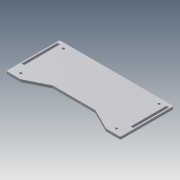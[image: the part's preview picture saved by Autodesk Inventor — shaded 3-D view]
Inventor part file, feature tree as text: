
AUTODESK INVENTOR PART (.ipt)
format: ipt  version: 2014 (Build 180170000, 170)  size: 132,608 bytes
history: native  units: mm
features: extrude x3, sketch x3, fillet x1
ambient origin geometry x8: Origin, YZ Plane, XZ Plane, XY Plane, X Axis, Y Axis, Z Axis, Center Point
bodies: Solid1 (feature_tree)
feature tree (7):
  extrude  "Extrusion1"  Depth=268.0mm
  extrude  "Extrusion2"  Depth=25.0mm
  extrude  "Extrusion5"  Depth=2.0mm
  fillet  "Fillet1"  Radius=3.0mm
  sketch  "Sketch1"  dims[d1=125.0mm d2=268.0mm]
  sketch  "Sketch2"  dims[d4=6.0mm d5=0.0mm d6=25.0mm]
  sketch  "Sketch7"  dims[d7=34.0mm d9=50.0mm d10=3.0mm d11=0.0mm d47=34.0mm d48=21.5mm d49=21.5mm d50=12.5mm d51=12.5mm d56=2.875mm d57=6.25mm d58=2.875mm d59=8.0mm d60=8.0mm d61=5.4mm d62=84.0mm d63=10.0mm d64=0.0mm d65=2.0mm]
